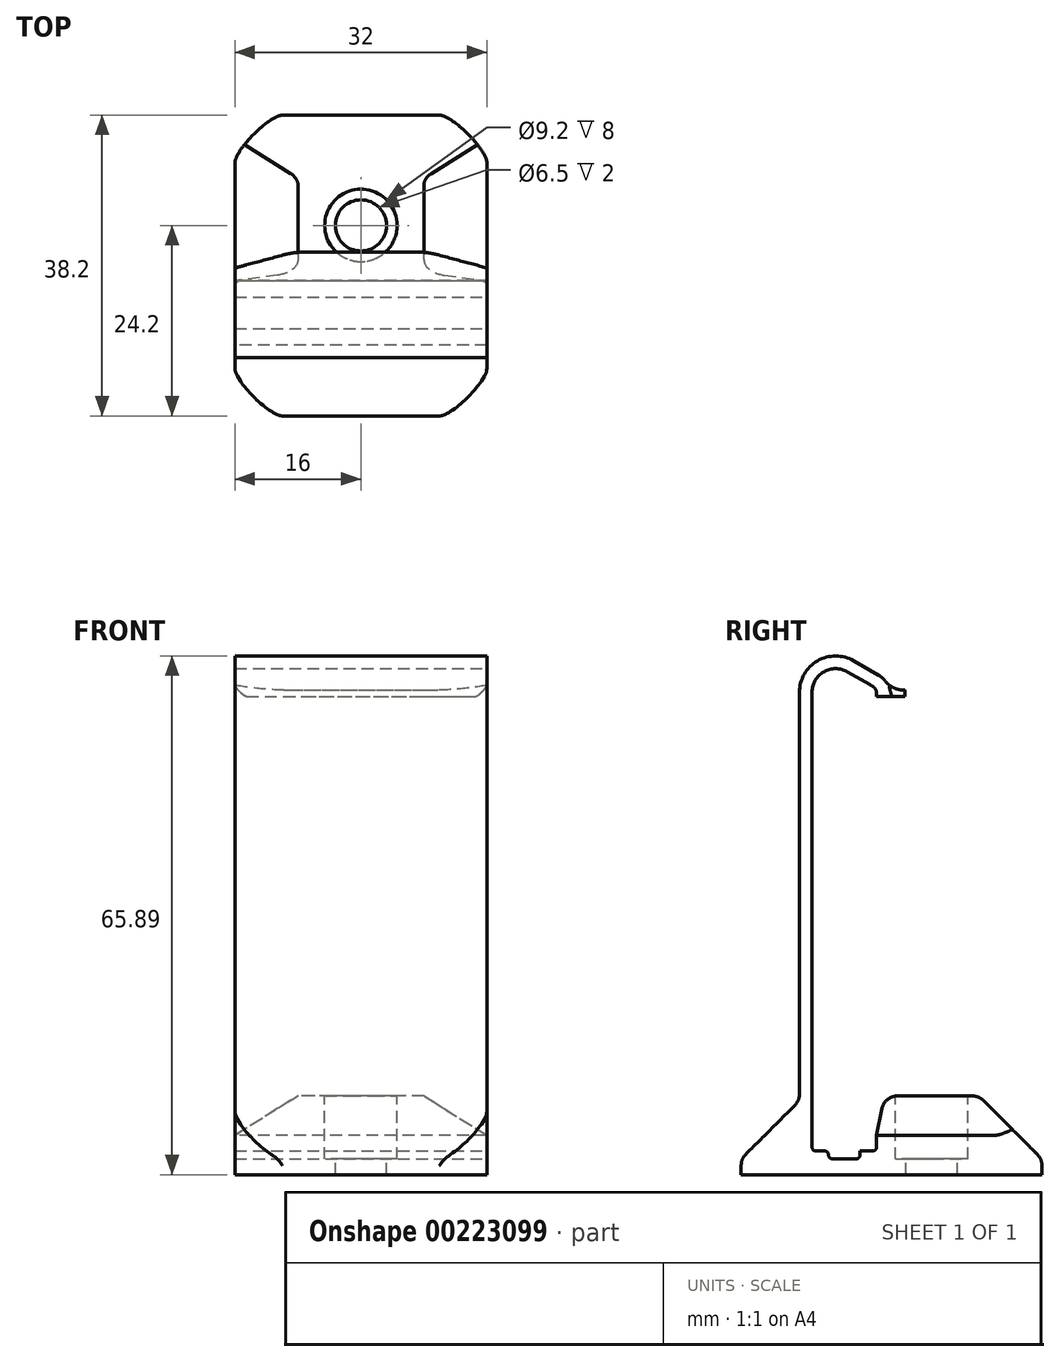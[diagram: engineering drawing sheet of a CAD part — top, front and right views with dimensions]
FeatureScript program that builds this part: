
annotation { "Feature Type Name" : "Feature", "Feature Type Description" : "" }
export const myFeature = defineFeature(function(context is Context, id is Id, definition is map)
    precondition{}
    {
        {
            var Q0;
            Q0=qCreatedBy(makeId("Right.planeOp"),FACE);
            var sketch = newSketch(context, id + "F0", { "sketchPlane" : qUnion([Q0])});
            skLineSegment(sketch, "E0.bottom", {"start": v(-4.1, 0) * mm, "end": v(4.1, 0) * mm});
            skLineSegment(sketch, "E0.top", {"start": v(-4.1, 58.75) * mm, "end": v(4.1, 58.75) * mm});
            skLineSegment(sketch, "E0.left", {"start": v(-4.1, 0) * mm, "end": v(-4.1, 58.75) * mm});
            skLineSegment(sketch, "E0.right", {"start": v(4.1, 0) * mm, "end": v(4.1, 58.75) * mm});
            skSolve(sketch);
        }
        {
            var Q0;
            Q0=qCreatedBy(makeId("Right.planeOp"),FACE);
            var sketch = newSketch(context, id + "F1", { "sketchPlane" : qUnion([Q0])});
            skLineSegment(sketch, "E1", {"start": v(-4.1, 6.4) * mm, "end": v(-5.7, 6.4) * mm});
            skLineSegment(sketch, "E2", {"start": v(-5.7, 6.4) * mm, "end": v(-13.1, -1) * mm});
            skLineSegment(sketch, "E3", {"start": v(-13.1, -1) * mm, "end": v(-13.1, -3) * mm});
            skLineSegment(sketch, "E4", {"start": v(-13.1, -3) * mm, "end": v(25.1, -3) * mm});
            skLineSegment(sketch, "E5", {"start": v(25.1, -3) * mm, "end": v(25.1, -1) * mm});
            skLineSegment(sketch, "E6", {"start": v(25.1, -1) * mm, "end": v(17.1, 7) * mm});
            skLineSegment(sketch, "E7", {"start": v(17.1, 7) * mm, "end": v(4.1, 7) * mm});
            skLineSegment(sketch, "E8", {"start": v(4.1, 7) * mm, "end": v(4.1, 0) * mm});
            skLineSegment(sketch, "E9", {"start": v(4.1, 0) * mm, "end": v(-4.1, 0) * mm});
            skLineSegment(sketch, "E10", {"start": v(-4.1, 0) * mm, "end": v(-4.1, 6.4) * mm});
            skSolve(sketch);
        }
        {
            var Q0;
            Q0=qSketchRegion(id+"F1",true);
            extrude(context, id + "F2", {"entities" : qUnion([Q0]), "endBound" : BoundingType.SYMMETRIC, "depth" : 32 * mm});
        }
        {
            var Q0;
            Q0=makeQuery(id+"F2.opExtrude","CAP_FACE",FACE,{"disambiguationData":[OSD([sQuery(id+"F1.wireOp",EDGE,"E1"),sQuery(id+"F1.wireOp",EDGE,"E2"),sQuery(id+"F1.wireOp",EDGE,"E3"),sQuery(id+"F1.wireOp",EDGE,"E4"),sQuery(id+"F1.wireOp",EDGE,"E5"),sQuery(id+"F1.wireOp",EDGE,"E6"),sQuery(id+"F1.wireOp",EDGE,"E7"),sQuery(id+"F1.wireOp",EDGE,"E8"),sQuery(id+"F1.wireOp",EDGE,"E9"),sQuery(id+"F1.wireOp",EDGE,"E10")])],"isStart":false});
            var sketch = newSketch(context, id + "F3", { "sketchPlane" : qUnion([Q0])});
            skLineSegment(sketch, "E11", {"start": v(-5.7, 6.4) * mm, "end": v(-4.1, 6.4) * mm});
            skLineSegment(sketch, "E12", {"start": v(-4.1, 6.4) * mm, "end": v(-4.1, 58.29) * mm});
            skLineSegment(sketch, "E13", {"start": v(0.4, 60.89) * mm, "end": v(3.6, 59.04) * mm});
            skLineSegment(sketch, "E14", {"start": v(4.1, 58.17) * mm, "end": v(4.1, 57.75) * mm});
            skLineSegment(sketch, "E15", {"start": v(4.1, 57.75) * mm, "end": v(5.7, 57.75) * mm});
            skLineSegment(sketch, "E16", {"start": v(5.7, 57.75) * mm, "end": v(5.7, 58.17) * mm});
            skLineSegment(sketch, "E17", {"start": v(4.4, 60.42) * mm, "end": v(1.2, 62.27) * mm});
            skLineSegment(sketch, "E18", {"start": v(-5.7, 58.29) * mm, "end": v(-5.7, 6.4) * mm});
            skArc(sketch, "E19", {"start": v(0.4, 60.89) * mm, "mid": v(-2.6, 60.89) * mm, "end": v(-4.1, 58.29) * mm});
            skArc(sketch, "E20", {"start": v(1.2, 62.27) * mm, "mid": v(-3.4, 62.27) * mm, "end": v(-5.7, 58.29) * mm});
            skArc(sketch, "E21", {"start": v(5.7, 58.17) * mm, "mid": v(5.35, 59.47) * mm, "end": v(4.4, 60.42) * mm});
            skArc(sketch, "E22", {"start": v(4.1, 58.17) * mm, "mid": v(3.97, 58.67) * mm, "end": v(3.6, 59.04) * mm});
            skLineSegment(sketch, "E23", {"start": v(3.6, 59.04) * mm, "end": v(4.1, 58.75) * mm, "construction": true});
            skLineSegment(sketch, "E24", {"start": v(4.1, 58.75) * mm, "end": v(4.1, 58.17) * mm, "construction": true});
            skLineSegment(sketch, "E25", {"start": v(4.1, 58.75) * mm, "end": v(-4.1, 58.29) * mm, "construction": true});
            skSolve(sketch);
        }
        {
            var Q0;
            Q0=qSketchRegion(id+"F3",true);
            var Q1;
            Q1=makeQuery(id+"F2.opExtrude","CAP_FACE",FACE,{"disambiguationData":[OSD([sQuery(id+"F1.wireOp",EDGE,"E1"),sQuery(id+"F1.wireOp",EDGE,"E2"),sQuery(id+"F1.wireOp",EDGE,"E3"),sQuery(id+"F1.wireOp",EDGE,"E4"),sQuery(id+"F1.wireOp",EDGE,"E5"),sQuery(id+"F1.wireOp",EDGE,"E6"),sQuery(id+"F1.wireOp",EDGE,"E7"),sQuery(id+"F1.wireOp",EDGE,"E8"),sQuery(id+"F1.wireOp",EDGE,"E9"),sQuery(id+"F1.wireOp",EDGE,"E10")])],"isStart":true});
            extrude(context, id + "F4", {"entities" : qUnion([Q0]), "operationType" : NewBodyOperationType.ADD, "endBound" : BoundingType.UP_TO_SURFACE, "oppositeDirection" : true, "endBoundEntityFace" : qUnion([Q1]), "depth" : 25 * mm});
        }
        {
            var Q0;
            Q0=makeQuery(id+"F4.boolean.opBoolean","MERGE",FACE,{"derivedFrom":[makeQuery(id+"F2.opExtrude","CAP_FACE",FACE,{"disambiguationData":[OSD([sQuery(id+"F1.wireOp",EDGE,"E1"),sQuery(id+"F1.wireOp",EDGE,"E2"),sQuery(id+"F1.wireOp",EDGE,"E3"),sQuery(id+"F1.wireOp",EDGE,"E4"),sQuery(id+"F1.wireOp",EDGE,"E5"),sQuery(id+"F1.wireOp",EDGE,"E6"),sQuery(id+"F1.wireOp",EDGE,"E7"),sQuery(id+"F1.wireOp",EDGE,"E8"),sQuery(id+"F1.wireOp",EDGE,"E9"),sQuery(id+"F1.wireOp",EDGE,"E10")])],"isStart":false}),makeQuery(id+"F4.opExtrude","CAP_FACE",FACE,{"disambiguationData":[OSD([sQuery(id+"F3.wireOp",EDGE,"E11"),sQuery(id+"F3.wireOp",EDGE,"E12"),sQuery(id+"F3.wireOp",EDGE,"E13"),sQuery(id+"F3.wireOp",EDGE,"E14"),sQuery(id+"F3.wireOp",EDGE,"E15"),sQuery(id+"F3.wireOp",EDGE,"E16"),sQuery(id+"F3.wireOp",EDGE,"E17"),sQuery(id+"F3.wireOp",EDGE,"E18"),sQuery(id+"F3.wireOp",EDGE,"E19"),sQuery(id+"F3.wireOp",EDGE,"E20"),sQuery(id+"F3.wireOp",EDGE,"E21"),sQuery(id+"F3.wireOp",EDGE,"E22")])],"isStart":true})]});
            var sketch = newSketch(context, id + "F5", { "sketchPlane" : qUnion([Q0])});
            skLineSegment(sketch, "E26.bottom", {"start": v(-2, 0) * mm, "end": v(2, 0) * mm});
            skLineSegment(sketch, "E26.top", {"start": v(-2, -1) * mm, "end": v(2, -1) * mm});
            skLineSegment(sketch, "E26.left", {"start": v(-2, 0) * mm, "end": v(-2, -1) * mm});
            skLineSegment(sketch, "E26.right", {"start": v(2, 0) * mm, "end": v(2, -1) * mm});
            skLineSegment(sketch, "E27", {"start": v(-4.1, 0) * mm, "end": v(-2, 0) * mm});
            skLineSegment(sketch, "E28", {"start": v(2, 0) * mm, "end": v(4.1, 0) * mm});
            skSolve(sketch);
        }
        {
            var Q0;
            Q0=qSketchRegion(id+"F5",true);
            extrude(context, id + "F6", {"entities" : qUnion([Q0]), "operationType" : NewBodyOperationType.REMOVE, "endBound" : BoundingType.THROUGH_ALL, "oppositeDirection" : true, "depth" : 25 * mm});
        }
        {
            var Q0;
            Q0=makeQuery(id+"F2.opExtrude","SWEPT_EDGE",EDGE,{"disambiguationData":[OSD([sQuery(id+"F1.wireOp",EDGE,"E7"),sQuery(id+"F1.wireOp",EDGE,"E8")])]});
            chamfer(context, id + "F7", {"entities" : qUnion([Q0]), "chamferType" : ChamferType.TWO_OFFSETS, "width1" : 5 * mm, "oppositeDirection" : false, "width2" : 1 * mm, "tangentPropagation" : true});
        }
        {
            var Q0;
            Q0=makeQuery(id+"F2.opExtrude","SWEPT_FACE",FACE,{"disambiguationData":[OSD([sQuery(id+"F1.wireOp",EDGE,"E7")])]});
            var sketch = newSketch(context, id + "F8", { "sketchPlane" : qUnion([Q0])});
            skCircle(sketch, "E29", {"center": v(0, 11.1) * mm, "radius": 4.6 * mm});
            skLineSegment(sketch, "E30", {"start": v(0, 6.5) * mm, "end": v(0, 5.1) * mm, "construction": true});
            skLineSegment(sketch, "E31", {"start": v(0, 15.7) * mm, "end": v(0, 17.1) * mm, "construction": true});
            skSolve(sketch);
        }
        {
            var Q0;
            Q0=qSketchRegion(id+"F8",true);
            extrude(context, id + "F9", {"entities" : qUnion([Q0]), "operationType" : NewBodyOperationType.REMOVE, "oppositeDirection" : true, "depth" : 8 * mm});
        }
        {
            var Q0;
            Q0=makeQuery(id+"F9.boolean.opBoolean","COPY",FACE,{"derivedFrom":makeQuery(id+"F9.opExtrude","CAP_FACE",FACE,{"disambiguationData":[OSD([sQuery(id+"F8.wireOp",EDGE,"E29")])],"isStart":false})});
            var sketch = newSketch(context, id + "F10", { "sketchPlane" : qUnion([Q0])});
            skCircle(sketch, "E32", {"center": v(0, 11.1) * mm, "radius": 3.25 * mm});
            skSolve(sketch);
        }
        {
            var Q0;
            Q0=qSketchRegion(id+"F10",true);
            extrude(context, id + "F11", {"entities" : qUnion([Q0]), "operationType" : NewBodyOperationType.REMOVE, "endBound" : BoundingType.UP_TO_NEXT, "oppositeDirection" : true, "depth" : 25 * mm});
        }
        {
            var Q0;
            Q0=makeQuery(id+"F2.opExtrude","SWEPT_EDGE",EDGE,{"disambiguationData":[OSD([sQuery(id+"F1.wireOp",EDGE,"E9"),sQuery(id+"F1.wireOp",EDGE,"E10")])]});
            var Q1;
            Q1=makeQuery(id+"F2.opExtrude","SWEPT_EDGE",EDGE,{"disambiguationData":[OSD([sQuery(id+"F1.wireOp",EDGE,"E8"),sQuery(id+"F1.wireOp",EDGE,"E9")])]});
            var Q2;
            Q2=makeQuery(id+"F2.opExtrude","SWEPT_EDGE",EDGE,{"disambiguationData":[OSD([sQuery(id+"F1.wireOp",EDGE,"E7"),sQuery(id+"F1.wireOp",EDGE,"E8")])]});
            var Q3;
            Q3=makeQuery(id+"F6.boolean.opBoolean","COPY",EDGE,{"derivedFrom":makeQuery(id+"F6.opExtrude","SWEPT_EDGE",EDGE,{"disambiguationData":[OSD([sQuery(id+"F5.wireOp",EDGE,"E26.top"),sQuery(id+"F5.wireOp",EDGE,"E26.right")])]})});
            var Q4;
            Q4=makeQuery(id+"F6.boolean.opBoolean","COPY",EDGE,{"derivedFrom":makeQuery(id+"F6.opExtrude","SWEPT_EDGE",EDGE,{"disambiguationData":[OSD([sQuery(id+"F5.wireOp",EDGE,"E26.top"),sQuery(id+"F5.wireOp",EDGE,"E26.left")])]})});
            var Q5;
            Q5=makeQuery(id+"F6.boolean.opBoolean","COPY",EDGE,{"derivedFrom":makeQuery(id+"F6.opExtrude","SWEPT_EDGE",EDGE,{"disambiguationData":[OSD([sQuery(id+"F5.wireOp",EDGE,"E26.bottom"),sQuery(id+"F5.wireOp",EDGE,"E26.right"),sQuery(id+"F5.wireOp",EDGE,"E28")])]})});
            var Q6;
            Q6=makeQuery(id+"F6.boolean.opBoolean","COPY",EDGE,{"derivedFrom":makeQuery(id+"F6.opExtrude","SWEPT_EDGE",EDGE,{"disambiguationData":[OSD([sQuery(id+"F5.wireOp",EDGE,"E26.bottom"),sQuery(id+"F5.wireOp",EDGE,"E26.left"),sQuery(id+"F5.wireOp",EDGE,"E27")])]})});
            fillet(context, id + "F12", {"entities" : qUnion([Q0, Q1, Q2, Q3, Q4, Q5, Q6]), "radius" : .5 * mm, "tangentPropagation" : true, "allowEdgeOverflow" : false});
        }
        {
            var Q0;
            Q0=makeQuery(id+"F2.opExtrude","SWEPT_EDGE",EDGE,{"disambiguationData":[OSD([sQuery(id+"F1.wireOp",EDGE,"E5"),sQuery(id+"F1.wireOp",EDGE,"E6")])]});
            var Q1;
            Q1=makeQuery(id+"F2.opExtrude","SWEPT_EDGE",EDGE,{"disambiguationData":[OSD([sQuery(id+"F1.wireOp",EDGE,"E6"),sQuery(id+"F1.wireOp",EDGE,"E7")])]});
            var Q2;
            {var subQ0=sQuery(id+"F1.wireOp",EDGE,"E2");Q2=makeQuery(id+"F4.boolean.opBoolean","MERGE",EDGE,{"derivedFrom":[makeQuery(id+"F2.opExtrude","SWEPT_EDGE",EDGE,{"disambiguationData":[OSD([sQuery(id+"F1.wireOp",EDGE,"E1"),subQ0])]}),makeQuery(id+"F4.opExtrude","SWEPT_EDGE",EDGE,{"disambiguationData":[OSD([subQ0,sQuery(id+"F3.wireOp",EDGE,"E11"),sQuery(id+"F3.wireOp",EDGE,"E18")])]})]});}
            var Q3;
            Q3=makeQuery(id+"F2.opExtrude","SWEPT_EDGE",EDGE,{"disambiguationData":[OSD([sQuery(id+"F1.wireOp",EDGE,"E2"),sQuery(id+"F1.wireOp",EDGE,"E3")])]});
            var Q4;
            {var subQ0=sQuery(id+"F1.wireOp",EDGE,"E7");Q4=makeQuery(id+"F7.opChamfer","BLEND_EDGE",EDGE,{"blendedFrom":[makeQuery(id+"F2.opExtrude","SWEPT_EDGE",EDGE,{"disambiguationData":[OSD([subQ0,sQuery(id+"F1.wireOp",EDGE,"E8")])]}),makeQuery(id+"F2.opExtrude","SWEPT_FACE",FACE,{"disambiguationData":[OSD([subQ0])]})],"blendedInto":[makeQuery(id+"F2.opExtrude","SWEPT_FACE",FACE,{"disambiguationData":[OSD([subQ0])]})]});}
            fillet(context, id + "F13", {"entities" : qUnion([Q0, Q1, Q2, Q3, Q4]), "radius" : 2 * mm, "tangentPropagation" : true, "allowEdgeOverflow" : false});
        }
        {
            var Q0;
            Q0=makeQuery(id+"F2.opExtrude","CAP_EDGE",EDGE,{"disambiguationData":[OSD([sQuery(id+"F1.wireOp",EDGE,"E3")])],"isStart":false});
            var Q1;
            Q1=makeQuery(id+"F2.opExtrude","CAP_EDGE",EDGE,{"disambiguationData":[OSD([sQuery(id+"F1.wireOp",EDGE,"E5")])],"isStart":false});
            var Q2;
            Q2=makeQuery(id+"F2.opExtrude","CAP_EDGE",EDGE,{"disambiguationData":[OSD([sQuery(id+"F1.wireOp",EDGE,"E5")])],"isStart":true});
            var Q3;
            Q3=makeQuery(id+"F2.opExtrude","CAP_EDGE",EDGE,{"disambiguationData":[OSD([sQuery(id+"F1.wireOp",EDGE,"E3")])],"isStart":true});
            fillet(context, id + "F14", {"entities" : qUnion([Q0, Q1, Q2, Q3]), "radius" : 6 * mm, "rho" : .2, "crossSection" : FilletCrossSection.CONIC, "allowEdgeOverflow" : false});
        }
        {
            var Q0;
            Q0=makeQuery(id+"F2.opExtrude","CAP_EDGE",EDGE,{"disambiguationData":[OSD([sQuery(id+"F1.wireOp",EDGE,"E7")])],"isStart":true});
            var Q1;
            Q1=makeQuery(id+"F2.opExtrude","CAP_EDGE",EDGE,{"disambiguationData":[OSD([sQuery(id+"F1.wireOp",EDGE,"E7")])],"isStart":false});
            chamfer(context, id + "F15", {"entities" : qUnion([Q0, Q1]), "chamferType" : ChamferType.TWO_OFFSETS, "width1" : 8 * mm, "oppositeDirection" : false, "width2" : 5 * mm});
        }
        {
            var Q0;
            Q0=makeQuery(id+"F4.opExtrude","SWEPT_FACE",FACE,{"disambiguationData":[OSD([sQuery(id+"F3.wireOp",EDGE,"E15")])]});
            var sketch = newSketch(context, id + "F16", { "sketchPlane" : qUnion([Q0])});
            skLineSegment(sketch, "E33", {"start": v(-16, -5.7) * mm, "end": v(-9.8, -7.36) * mm});
            skLineSegment(sketch, "E34", {"start": v(-7.22, -7.7) * mm, "end": v(7.22, -7.7) * mm});
            skLineSegment(sketch, "E35", {"start": v(9.8, -7.36) * mm, "end": v(16, -5.7) * mm});
            skPoint(sketch, "E36.visualSharp", {"position": v(8.54, -7.7) * mm});
            skArc(sketch, "E36.filletArc", {"start": v(7.22, -7.7) * mm, "mid": v(8.52, -7.61) * mm, "end": v(9.8, -7.36) * mm});
            skPoint(sketch, "E37.visualSharp", {"position": v(-8.54, -7.7) * mm});
            skArc(sketch, "E37.filletArc", {"start": v(-9.8, -7.36) * mm, "mid": v(-8.52, -7.61) * mm, "end": v(-7.22, -7.7) * mm});
            skLineSegment(sketch, "E38", {"start": v(16, -5.7) * mm, "end": v(16, -4.1) * mm});
            skLineSegment(sketch, "E39", {"start": v(16, -4.1) * mm, "end": v(-16, -4.1) * mm});
            skLineSegment(sketch, "E40", {"start": v(-16, -4.1) * mm, "end": v(-16, -5.7) * mm});
            skSolve(sketch);
        }
        {
            var Q0;
            Q0=qSketchRegion(id+"F16",true);
            extrude(context, id + "F17", {"entities" : qUnion([Q0]), "operationType" : NewBodyOperationType.ADD, "oppositeDirection" : true, "depth" : .8 * mm});
        }
        {
            var Q0;
            Q0=makeQuery(id+"F17.boolean.opBoolean","INTERSECT",EDGE,{"derivedFrom":[makeQuery(id+"F4.opExtrude","SWEPT_FACE",FACE,{"disambiguationData":[OSD([sQuery(id+"F3.wireOp",EDGE,"E21")])]}),makeQuery(id+"F17.opExtrude","CAP_FACE",FACE,{"disambiguationData":[OSD([sQuery(id+"F16.wireOp",EDGE,"E33"),sQuery(id+"F16.wireOp",EDGE,"E34"),sQuery(id+"F16.wireOp",EDGE,"E35"),sQuery(id+"F16.wireOp",EDGE,"E36.filletArc"),sQuery(id+"F16.wireOp",EDGE,"E37.filletArc"),sQuery(id+"F16.wireOp",EDGE,"E38"),sQuery(id+"F16.wireOp",EDGE,"E39"),sQuery(id+"F16.wireOp",EDGE,"E40")])],"isStart":false})]});
            fillet(context, id + "F18", {"entities" : qUnion([Q0]), "radius" : 3 * mm, "tangentPropagation" : true, "allowEdgeOverflow" : false});
        }
        {
            var Q0;
            Q0=makeQuery(id+"F4.opExtrude","CAP_EDGE",EDGE,{"disambiguationData":[OSD([sQuery(id+"F3.wireOp",EDGE,"E15")])],"isStart":true});
            var Q1;
            Q1=makeQuery(id+"F4.opExtrude","CAP_EDGE",EDGE,{"disambiguationData":[OSD([sQuery(id+"F3.wireOp",EDGE,"E15")])],"isStart":false});
            fillet(context, id + "F19", {"entities" : qUnion([Q0, Q1]), "radius" : 1.5 * mm, "tangentPropagation" : true, "rho" : .2, "crossSection" : FilletCrossSection.CONIC, "allowEdgeOverflow" : false});
        }
    });
